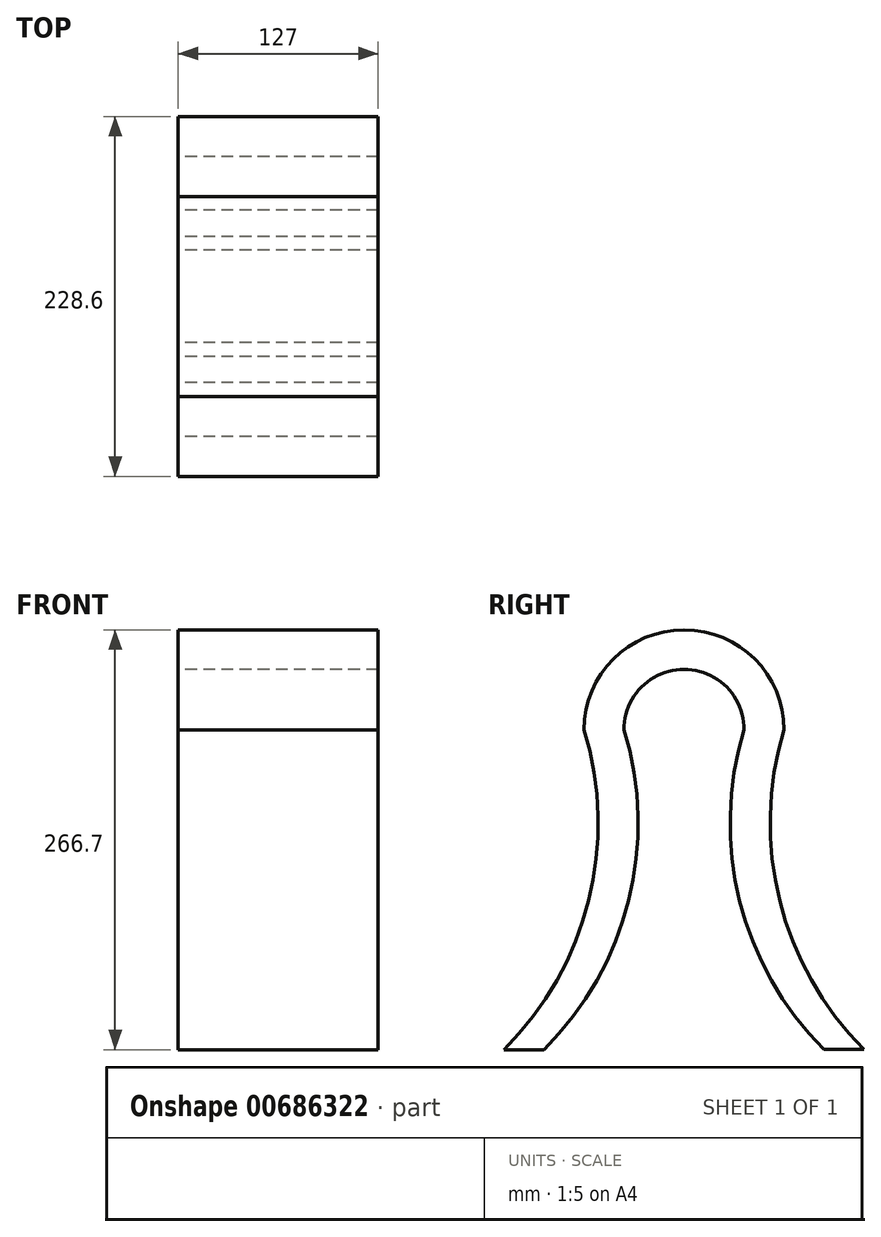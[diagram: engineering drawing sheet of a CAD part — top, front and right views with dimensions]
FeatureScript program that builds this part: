
annotation { "Feature Type Name" : "Feature", "Feature Type Description" : "" }
export const myFeature = defineFeature(function(context is Context, id is Id, definition is map)
    precondition{}
    {
        {
            var Q0;
            Q0=qCreatedBy(makeId("Right.planeOp"),FACE);
            var sketch = newSketch(context, id + "F0", { "sketchPlane" : qUnion([Q0])});
            skLineSegment(sketch, "E0.top", {"start": v(63.5, -101.6) * mm, "end": v(-63.5, -101.6) * mm});
            skPoint(sketch, "E0.middle", {"position": v(0, 0) * mm});
            skArc(sketch, "E1", {"start": v(63.5, 101.6) * mm, "mid": v(0, 165.1) * mm, "end": v(-63.5, 101.6) * mm});
            skArc(sketch, "E2", {"start": v(63.5, 101.6) * mm, "mid": v(60.74, -6.97) * mm, "end": v(114.3, -101.45) * mm});
            skLineSegment(sketch, "E3", {"start": v(63.5, -101.6) * mm, "end": v(114.3, -101.45) * mm});
            skLineSegment(sketch, "E4", {"start": v(-63.5, -101.6) * mm, "end": v(-114.3, -101.6) * mm});
            skArc(sketch, "E5", {"start": v(-114.3, -101.6) * mm, "mid": v(-60.7, -7.05) * mm, "end": v(-63.5, 101.6) * mm});
            skLineSegment(sketch, "E6", {"start": v(0, 101.6) * mm, "end": v(-63.5, 101.6) * mm});
            skLineSegment(sketch, "E7", {"start": v(0, 101.6) * mm, "end": v(63.5, 101.6) * mm});
            skArc(sketch, "E8", {"start": v(-88.9, -101.6) * mm, "mid": v(-35.3, -7.05) * mm, "end": v(-38.1, 101.6) * mm});
            skArc(sketch, "E9", {"start": v(38.1, 101.6) * mm, "mid": v(35.32, -7.01) * mm, "end": v(88.9, -101.53) * mm});
            skArc(sketch, "E10", {"start": v(38.1, 101.6) * mm, "mid": v(0, 140.04) * mm, "end": v(-38.1, 101.6) * mm});
            skSolve(sketch);
        }
        {
            var Q0;
            {var subQ0=sQuery(id+"F0.wireOp",EDGE,"E1");Q0=makeQuery(id+"F0.imprint","IMPRINT",FACE,{"disambiguationData":[TD([[makeQuery(id+"F0.imprint","IMPRINT",EDGE,{"derivedFrom":subQ0}),1.0]])]});}
            var Q1;
            {var subQ0=sQuery(id+"F0.wireOp",EDGE,"E5");Q1=makeQuery(id+"F0.imprint","IMPRINT",FACE,{"disambiguationData":[TD([[makeQuery(id+"F0.imprint","IMPRINT",EDGE,{"derivedFrom":subQ0}),-1.0]])]});}
            var Q2;
            {var subQ0=sQuery(id+"F0.wireOp",EDGE,"E2");Q2=makeQuery(id+"F0.imprint","IMPRINT",FACE,{"disambiguationData":[TD([[makeQuery(id+"F0.imprint","IMPRINT",EDGE,{"derivedFrom":subQ0}),-1.0]])]});}
            extrude(context, id + "F1", {"entities" : qUnion([Q0, Q1, Q2]), "endBound" : BoundingType.SYMMETRIC, "depth" : 127 * mm, "offsetDistance" : 25.4 * mm});
        }
    });
